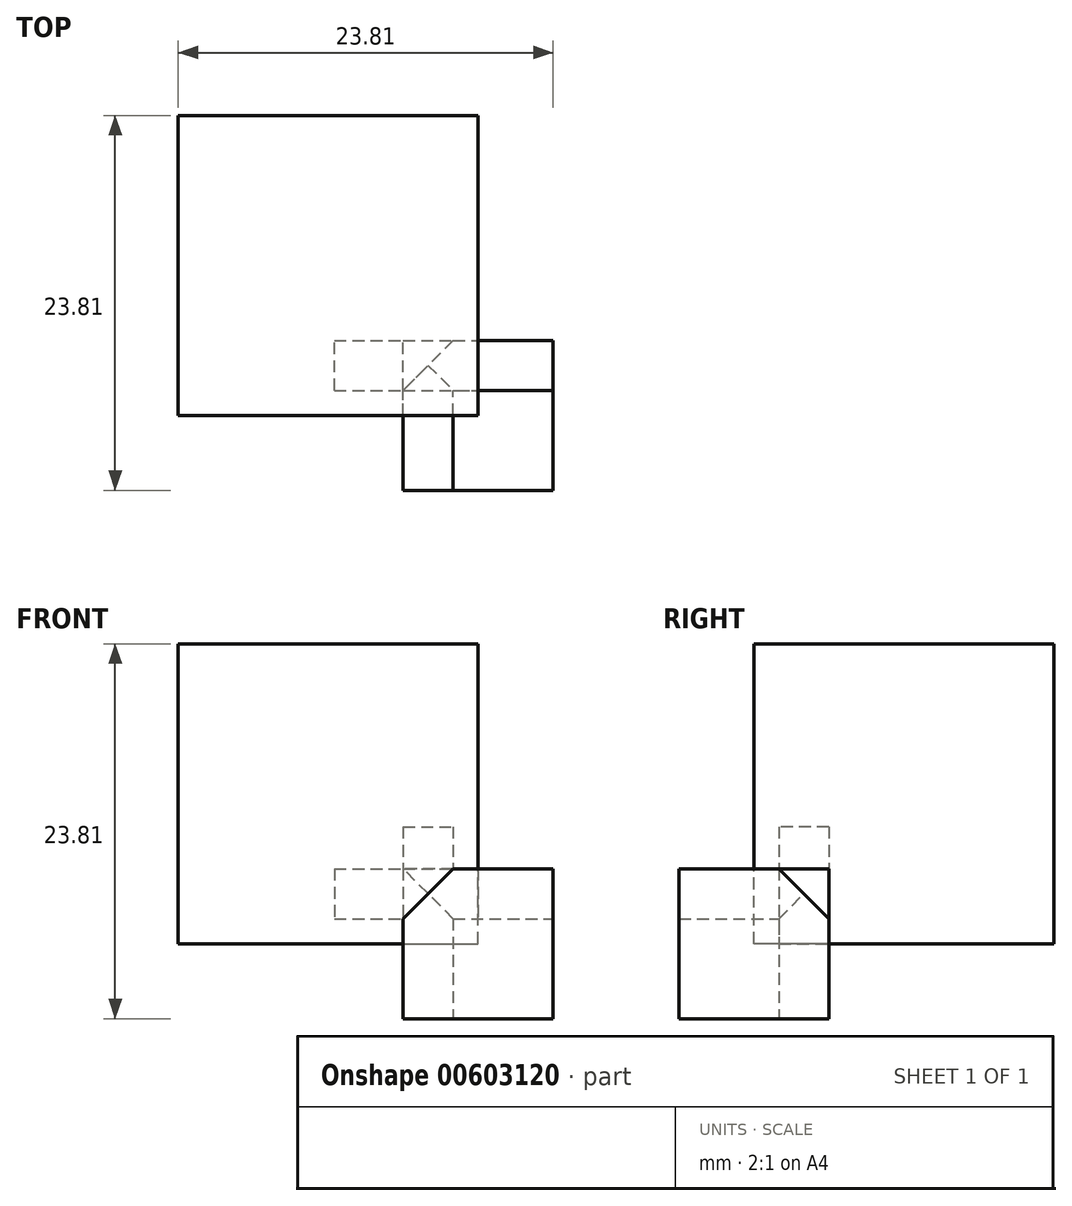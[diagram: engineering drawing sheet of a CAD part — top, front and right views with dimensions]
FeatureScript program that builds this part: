
annotation { "Feature Type Name" : "Feature", "Feature Type Description" : "" }
export const myFeature = defineFeature(function(context is Context, id is Id, definition is map)
    precondition{}
    {
        {
            var Q0;
            Q0=qCreatedBy(makeId("Front.planeOp"),FACE);
            var sketch = newSketch(context, id + "F0", { "sketchPlane" : qUnion([Q0])});
            skLineSegment(sketch, "E0.bottom", {"start": v(0, 0) * mm, "end": v(19.05, 0) * mm});
            skLineSegment(sketch, "E0.top", {"start": v(0, 19.05) * mm, "end": v(19.05, 19.05) * mm});
            skLineSegment(sketch, "E0.left", {"start": v(0, 0) * mm, "end": v(0, 19.05) * mm});
            skLineSegment(sketch, "E0.right", {"start": v(19.05, 0) * mm, "end": v(19.05, 19.05) * mm});
            skSolve(sketch);
        }
        {
            var Q0;
            Q0=qSketchRegion(id+"F0",true);
            extrude(context, id + "F1", {"entities" : qUnion([Q0]), "oppositeDirection" : true, "depth" : 19.05 * mm, "offsetDistance" : 25.4 * mm});
        }
        {
            var Q0;
            Q0=makeQuery(id+"F1.opExtrude","CAP_FACE",FACE,{"disambiguationData":[OSD([sQuery(id+"F0.wireOp",EDGE,"E0.bottom"),sQuery(id+"F0.wireOp",EDGE,"E0.top"),sQuery(id+"F0.wireOp",EDGE,"E0.left"),sQuery(id+"F0.wireOp",EDGE,"E0.right")])],"isStart":true});
            cPlane(context, id + "F2", {"entities" : qUnion([Q0]), "cplaneType" : CPlaneType.OFFSET, "offset" : 4.76 * mm, "oppositeDirection" : true, "width" : 152.4 * mm, "height" : 152.4 * mm});
        }
        {
            var Q0;
            Q0=qCreatedBy(id+"F2.planeOp",FACE);
            var sketch = newSketch(context, id + "F3", { "sketchPlane" : qUnion([Q0])});
            skLineSegment(sketch, "E1.bottom", {"start": v(17.46, 4.76) * mm, "end": v(23.81, 4.76) * mm});
            skLineSegment(sketch, "E1.top", {"start": v(14.29, -4.76) * mm, "end": v(23.81, -4.76) * mm});
            skLineSegment(sketch, "E1.left", {"start": v(14.29, 1.59) * mm, "end": v(14.29, -4.76) * mm});
            skLineSegment(sketch, "E1.right", {"start": v(23.81, 4.76) * mm, "end": v(23.81, -4.76) * mm});
            skLineSegment(sketch, "E2", {"start": v(14.29, 1.59) * mm, "end": v(17.46, 4.76) * mm});
            skPoint(sketch, "E3", {"position": v(19.05, 0) * mm});
            skPoint(sketch, "E3.positionSnap0", {"position": v(19.05, -4.76) * mm});
            skPoint(sketch, "E3.positionSnap1", {"position": v(23.81, 0) * mm});
            skSolve(sketch);
        }
        {
            var Q0;
            Q0=qSketchRegion(id+"F3",true);
            extrude(context, id + "F4", {"entities" : qUnion([Q0]), "depth" : 9.52 * mm, "offsetDistance" : 25.4 * mm});
        }
        {
            var Q0;
            Q0=makeQuery(id+"F4.opExtrude","SWEPT_FACE",FACE,{"disambiguationData":[OSD([sQuery(id+"F3.wireOp",EDGE,"E1.right")])]});
            var sketch = newSketch(context, id + "F5", { "sketchPlane" : qUnion([Q0])});
            skLineSegment(sketch, "E4", {"start": v(1.59, 4.76) * mm, "end": v(4.76, 1.59) * mm});
            skLineSegment(sketch, "E5", {"start": v(4.76, 1.59) * mm, "end": v(4.76, 4.76) * mm});
            skLineSegment(sketch, "E6", {"start": v(4.76, 4.76) * mm, "end": v(1.59, 4.76) * mm});
            skSolve(sketch);
        }
        {
            var Q0;
            Q0=qSketchRegion(id+"F5",true);
            var Q1;
            Q1 = qSketchRegion(id + "F7", true);
            extrude(context, id + "F6", {"entities" : qUnion([Q0, Q1]), "operationType" : NewBodyOperationType.REMOVE, "oppositeDirection" : true, "depth" : 13.9 * mm, "offsetDistance" : 25.4 * mm});
        }
        {
            var Q0;
            Q0=makeQuery(id+"F4.opExtrude","SWEPT_FACE",FACE,{"disambiguationData":[OSD([sQuery(id+"F3.wireOp",EDGE,"E1.top")])]});
            var sketch = newSketch(context, id + "F7", { "sketchPlane" : qUnion([Q0])});
            skLineSegment(sketch, "E7", {"start": v(14.29, -4.76) * mm, "end": v(14.29, -1.59) * mm});
            skLineSegment(sketch, "E8", {"start": v(17.46, -4.76) * mm, "end": v(14.29, -4.76) * mm});
            skLineSegment(sketch, "E9", {"start": v(17.46, -4.76) * mm, "end": v(14.29, -1.59) * mm});
            skLineSegment(sketch, "E10", {"start": v(14.29, -4.76) * mm, "end": v(17.46, -4.76) * mm});
            skLineSegment(sketch, "E11", {"start": v(14.29, -1.59) * mm, "end": v(14.29, -4.76) * mm});
            skSolve(sketch);
        }
        {
            var Q0;
            Q0=qSketchRegion(id+"F7",true);
            extrude(context, id + "F8", {"entities" : qUnion([Q0]), "operationType" : NewBodyOperationType.REMOVE, "oppositeDirection" : true, "depth" : 12.2 * mm});
        }
    });
